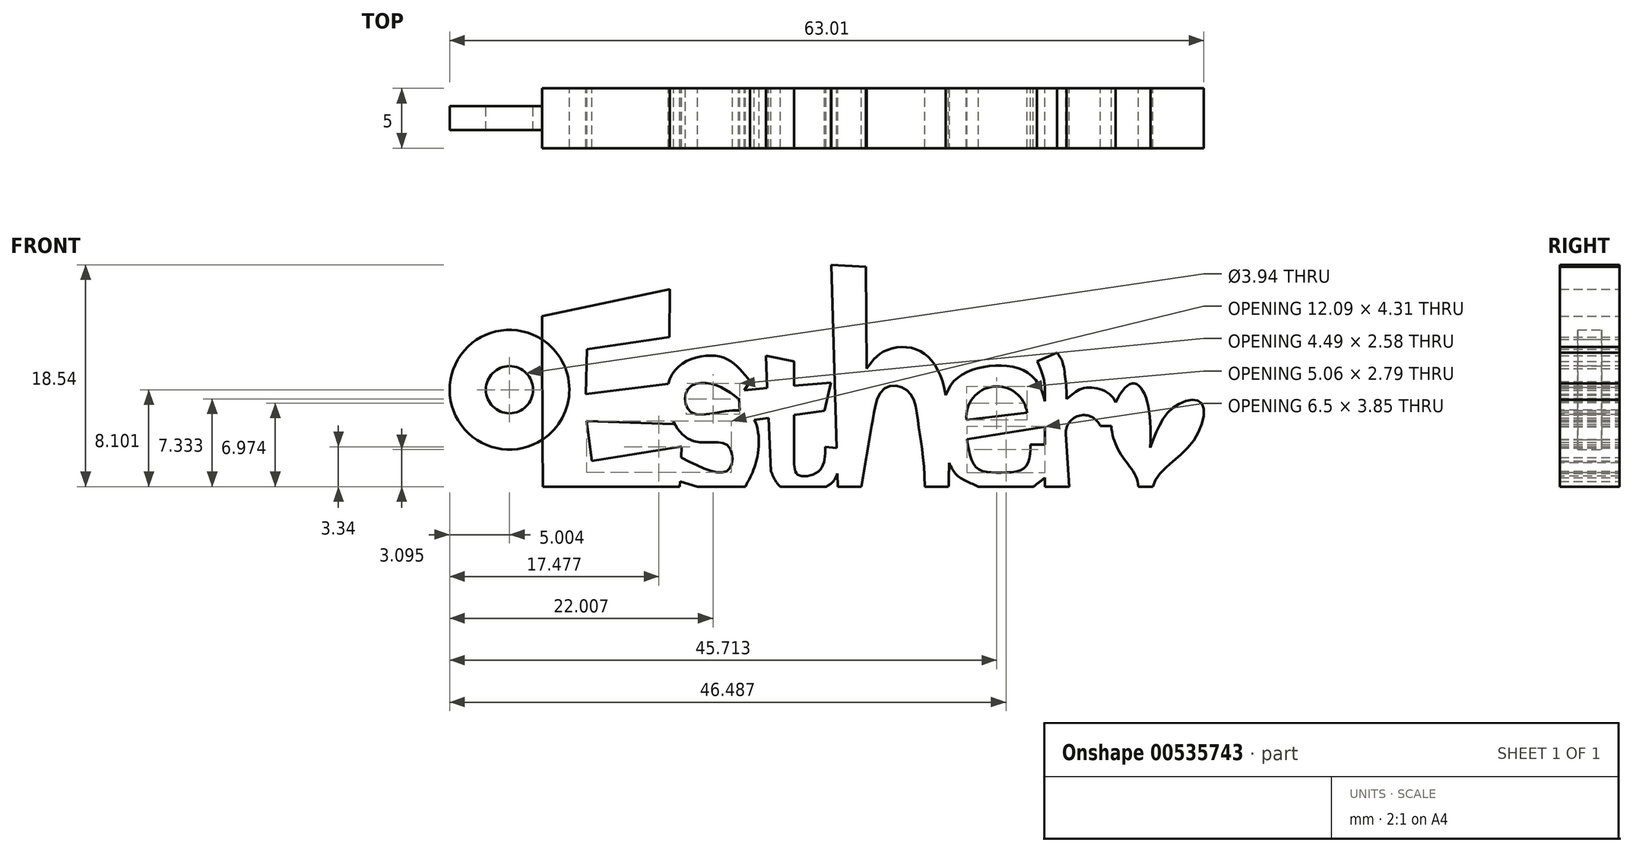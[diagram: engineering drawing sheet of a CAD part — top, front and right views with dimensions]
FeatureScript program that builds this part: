
annotation { "Feature Type Name" : "Feature", "Feature Type Description" : "" }
export const myFeature = defineFeature(function(context is Context, id is Id, definition is map)
    precondition{}
    {
        {
            var Q0;
            Q0=qCreatedBy(makeId("Front.planeOp"),FACE);
            var sketch = newSketch(context, id + "F0", { "sketchPlane" : qUnion([Q0])});
            skLineSegment(sketch, "E0", {"start": v(-25.3, 9.16) * mm, "end": v(-14.64, 11.43) * mm});
            skLineSegment(sketch, "E1", {"start": v(-14.64, 11.43) * mm, "end": v(-14.65, 7.42) * mm});
            skLineSegment(sketch, "E2", {"start": v(-14.65, 7.42) * mm, "end": v(-21.53, 6.42) * mm});
            skLineSegment(sketch, "E3", {"start": v(-21.53, 6.42) * mm, "end": v(-21.65, 2.67) * mm});
            skLineSegment(sketch, "E4", {"start": v(-21.65, 2.67) * mm, "end": v(-14.37, 3.56) * mm});
            skLineSegment(sketch, "E5", {"start": v(-14.37, 3.56) * mm, "end": v(-14.31, 0.15) * mm});
            skLineSegment(sketch, "E6", {"start": v(-14.31, 0.15) * mm, "end": v(-21.59, 0.43) * mm});
            skLineSegment(sketch, "E7", {"start": v(-21.59, 0.43) * mm, "end": v(-21.14, -2.93) * mm});
            skLineSegment(sketch, "E8", {"start": v(-21.14, -2.93) * mm, "end": v(-13.64, -1.7) * mm});
            skLineSegment(sketch, "E9", {"start": v(-13.64, -1.7) * mm, "end": v(-13.8, -5.07) * mm});
            skLineSegment(sketch, "E10", {"start": v(-13.8, -5.07) * mm, "end": v(-25.23, -5.07) * mm});
            skLineSegment(sketch, "E11", {"start": v(-25.23, -5.07) * mm, "end": v(-25.3, 9.16) * mm});
            skFitSpline(sketch, "E12", {"points": [v(-7.93, 3.73) * mm, v(-10.44, 5.8) * mm, v(-14.53, 4.12) * mm, v(-13.08, -1.09) * mm, v(-9.83, -1.6) * mm, v(-9.72, -3.67) * mm, v(-13.97, -2.49) * mm], "startDerivative": vector(-13.02, 17.28) * mm, "endDerivative": vector(-29.51, 15.15) * mm});
            skLineSegment(sketch, "E13", {"start": v(-13.97, -2.49) * mm, "end": v(-15.5, -5.07) * mm});
            skLineSegment(sketch, "E14", {"start": v(-15.5, -5.07) * mm, "end": v(-8.32, -5.07) * mm});
            skLineSegment(sketch, "E15", {"start": v(-7.93, 3.73) * mm, "end": v(-8.88, 2.27) * mm});
            skFitSpline(sketch, "E16", {"points": [v(-8.88, 2.27) * mm, v(-11.06, 3.5) * mm, v(-13.13, 3.05) * mm, v(-12.74, 1.1) * mm, v(-8.26, 1.19) * mm, v(-7.25, -2.27) * mm, v(-8.32, -5.07) * mm], "startDerivative": vector(-12.95, 9.86) * mm, "endDerivative": vector(-8.13, -15.9) * mm});
            skLineSegment(sketch, "E17", {"start": v(-8.4, 3) * mm, "end": v(-1.15, 3.61) * mm});
            skLineSegment(sketch, "E18", {"start": v(-1.15, 3.61) * mm, "end": v(-1.71, 1.26) * mm});
            skLineSegment(sketch, "E19", {"start": v(-8.88, 3) * mm, "end": v(-8.4, 3) * mm});
            skLineSegment(sketch, "E20", {"start": v(-6.6, 5.86) * mm, "end": v(-4.25, 5.39) * mm});
            skLineSegment(sketch, "E21", {"start": v(-4.25, 5.39) * mm, "end": v(-4.25, -3) * mm});
            skLineSegment(sketch, "E22", {"start": v(-6.6, 5.86) * mm, "end": v(-6.18, -3.8) * mm});
            skFitSpline(sketch, "E23", {"points": [v(-6.18, -3.8) * mm, v(-5.04, -5.32) * mm, v(-2.45, -5.32) * mm, v(-0.87, -4.5) * mm, v(-0.33, -2.33) * mm, v(-0.38, -1.86) * mm], "startDerivative": vector(3.98, -8.84) * mm, "endDerivative": vector(-0.72, 3.35) * mm});
            skLineSegment(sketch, "E24", {"start": v(-1.63, -1.74) * mm, "end": v(-0.38, -1.86) * mm});
            skFitSpline(sketch, "E25", {"points": [v(-4.25, -3) * mm, v(-3.89, -4.1) * mm, v(-2.14, -3.74) * mm, v(-1.63, -1.74) * mm], "startDerivative": vector(0.2, -4.88) * mm, "endDerivative": vector(0.09, 6.18) * mm});
            skLineSegment(sketch, "E26", {"start": v(-8.88, 3) * mm, "end": v(-8.71, 0.36) * mm});
            skLineSegment(sketch, "E27", {"start": v(-8.32, -5.07) * mm, "end": v(34.22, -5.07) * mm});
            skLineSegment(sketch, "E28", {"start": v(34.22, -5.07) * mm, "end": v(34.22, -5.7) * mm});
            skLineSegment(sketch, "E29", {"start": v(-1.71, 1.26) * mm, "end": v(-8.71, 0.36) * mm});
            skLineSegment(sketch, "E30", {"start": v(-1.14, 13.47) * mm, "end": v(-0.59, -5.32) * mm});
            skLineSegment(sketch, "E31", {"start": v(-0.59, -5.32) * mm, "end": v(1.37, -5.07) * mm});
            skLineSegment(sketch, "E32", {"start": v(1.37, -5.07) * mm, "end": v(2.25, 0) * mm});
            skLineSegment(sketch, "E33", {"start": v(-1.14, 13.47) * mm, "end": v(1.74, 13.3) * mm});
            skLineSegment(sketch, "E34", {"start": v(1.74, 13.3) * mm, "end": v(1.84, 4.79) * mm});
            skFitSpline(sketch, "E35", {"points": [v(2.25, 0) * mm, v(3.2, 3.04) * mm, v(5.27, 2.9) * mm, v(6.17, 0) * mm, v(6.69, -5.07) * mm], "startDerivative": vector(1.76, 9.63) * mm, "endDerivative": vector(0.27, -22.07) * mm});
            skFitSpline(sketch, "E36", {"points": [v(1.84, 4.79) * mm, v(3.2, 6.2) * mm, v(5.89, 6.43) * mm, v(8.1, 3.9) * mm, v(8.66, -5.07) * mm], "startDerivative": vector(6.3, 9.08) * mm, "endDerivative": vector(-0.74, -27.4) * mm});
            skLineSegment(sketch, "E37", {"start": v(10.22, -1.1) * mm, "end": v(17, 0) * mm});
            skFitSpline(sketch, "E38", {"points": [v(17, 0) * mm, v(15.82, 3.99) * mm, v(12.24, 5.02) * mm, v(8.85, 3.42) * mm, v(8.05, -0.91) * mm], "startDerivative": vector(-1.1, 14.93) * mm, "endDerivative": vector(-0.27, -18.01) * mm});
            skFitSpline(sketch, "E39", {"points": [v(8.05, -0.91) * mm, v(9.28, -4.02) * mm, v(11.16, -5.07) * mm], "startDerivative": vector(1.72, -6.44) * mm, "endDerivative": vector(4.58, -2.3) * mm});
            skLineSegment(sketch, "E40", {"start": v(15.5, -1.57) * mm, "end": v(17.07, -1.57) * mm});
            skArc(sketch, "E41", {"start": v(15.22, 1.1) * mm, "mid": v(12.4, 3.3) * mm, "end": v(10.16, 0.51) * mm});
            skLineSegment(sketch, "E42", {"start": v(10.16, 0.51) * mm, "end": v(15.22, 1.1) * mm});
            skFitSpline(sketch, "E43", {"points": [v(10.22, -1.1) * mm, v(10.98, -3.47) * mm, v(13.01, -3.9) * mm, v(15.08, -3.43) * mm, v(15.5, -1.57) * mm], "startDerivative": vector(1.46, -10.58) * mm, "endDerivative": vector(0.22, 9.33) * mm});
            skFitSpline(sketch, "E44", {"points": [v(17.07, -1.57) * mm, v(17.07, -3.83) * mm, v(15.74, -5.07) * mm], "startDerivative": vector(0.71, -4.73) * mm, "endDerivative": vector(-3.43, -2.68) * mm});
            skLineSegment(sketch, "E45", {"start": v(16.72, 3.15) * mm, "end": v(16.72, -5.07) * mm});
            skLineSegment(sketch, "E46", {"start": v(16.72, -5.07) * mm, "end": v(16.83, -5.26) * mm});
            skLineSegment(sketch, "E47", {"start": v(16.05, 5.41) * mm, "end": v(17.74, 6.12) * mm});
            skFitSpline(sketch, "E48", {"points": [v(17.74, 6.12) * mm, v(18.16, 5.39) * mm, v(18.53, 2.26) * mm], "startDerivative": vector(1.63, -2.78) * mm, "endDerivative": vector(0.11, -5.24) * mm});
            skFitSpline(sketch, "E49", {"points": [v(16.05, 5.41) * mm, v(16.4, 4.66) * mm, v(16.72, 3.15) * mm], "startDerivative": vector(1.1, -1.78) * mm, "endDerivative": vector(0.14, -3.33) * mm});
            skLineSegment(sketch, "E50", {"start": v(18.47, -0.68) * mm, "end": v(18.74, -5.07) * mm});
            skArc(sketch, "E51", {"start": v(21.33, 0) * mm, "mid": v(19.61, 0.87) * mm, "end": v(18.47, -0.68) * mm});
            skLineSegment(sketch, "E52", {"start": v(22.97, 0) * mm, "end": v(21.33, 0) * mm});
            skFitSpline(sketch, "E53", {"points": [v(18.53, 2.26) * mm, v(20.08, 3.18) * mm, v(22.36, 2.42) * mm, v(22.97, 0) * mm], "startDerivative": vector(5, 3.96) * mm, "endDerivative": vector(0.8, -6.84) * mm});
            skFitSpline(sketch, "E54", {"points": [v(24.52, -5.07) * mm, v(23.14, -2.47) * mm, v(22.3, 0.8) * mm, v(23.81, 3.5) * mm, v(24.8, 3.1) * mm, v(25.5, -1.82) * mm], "startDerivative": vector(-0.48, 14.78) * mm, "endDerivative": vector(-1.96, -25.42) * mm});
            skFitSpline(sketch, "E55", {"points": [v(25.5, -1.82) * mm, v(27.37, 1.49) * mm, v(29.71, 1.99) * mm, v(29.04, -1.34) * mm, v(25.72, -5.07) * mm], "startDerivative": vector(6.34, 15.81) * mm, "endDerivative": vector(-2.63, -13.8) * mm});
            skLineSegment(sketch, "E56", {"start": v(-25.29, 6.06) * mm, "end": v(-25.26, 0.05) * mm});
            skLineSegment(sketch, "E57.bottom", {"start": v(-25.29, 6.06) * mm, "end": v(-27.26, 6.06) * mm});
            skLineSegment(sketch, "E57.top", {"start": v(-25.29, 0) * mm, "end": v(-27.26, 0) * mm});
            skLineSegment(sketch, "E57.left", {"start": v(-25.29, 6.06) * mm, "end": v(-25.29, 0) * mm});
            skLineSegment(sketch, "E57.right", {"start": v(-27.26, 6.06) * mm, "end": v(-27.26, 0) * mm});
            skCircle(sketch, "E58", {"center": v(-28.02, 3.03) * mm, "radius": 1.97 * mm});
            skPoint(sketch, "E58.centerSnap0", {"position": v(-27.26, 3.03) * mm});
            skCircle(sketch, "E59", {"center": v(-28.02, 3.03) * mm, "radius": 5 * mm});
            skLineSegment(sketch, "E60", {"start": v(-13.78, -4.63) * mm, "end": v(-12.3, -5.07) * mm});
            skSolve(sketch);
        }
        {
            var Q0;
            Q0=makeQuery(id+"F0.imprint","IMPRINT",FACE,{"disambiguationData":[TD([[makeQuery(id+"F0.imprint","IMPRINT",EDGE,{"derivedFrom":sQuery(id+"F0.wireOp",EDGE,"E0")}),-1.0]])]});
            var Q1;
            {var subQ0=sQuery(id+"F0.wireOp",EDGE,"E14");var subQ1=sQuery(id+"F0.wireOp",EDGE,"E9");var subQ2=makeQuery(id+"F0.imprint","INTERSECT",VERTEX,{"derivedFrom":[subQ1,subQ0]});Q1=makeQuery(id+"F0.imprint","IMPRINT",FACE,{"disambiguationData":[TD([[makeQuery(id+"F0.imprint","IMPRINT",EDGE,{"disambiguationData":[TD([[subQ2,1.0]])],"derivedFrom":subQ1}),-1.0]])]});}
            var Q2;
            {var subQ10=sQuery(id+"F0.wireOp",EDGE,"E12");Q2=makeQuery(id+"F0.imprint","IMPRINT",FACE,{"disambiguationData":[TD([[makeQuery(id+"F0.imprint","IMPRINT",EDGE,{"derivedFrom":subQ10}),1.0]])]});}
            var Q3;
            {var subQ0=sQuery(id+"F0.wireOp",EDGE,"E19");Q3=makeQuery(id+"F0.imprint","IMPRINT",FACE,{"disambiguationData":[TD([[makeQuery(id+"F0.imprint","IMPRINT",EDGE,{"derivedFrom":subQ0}),-1.0]])]});}
            var Q4;
            {var subQ0=sQuery(id+"F0.wireOp",EDGE,"E26");var subQ1=sQuery(id+"F0.wireOp",EDGE,"E16");var subQ2=makeQuery(id+"F0.imprint","INTERSECT",VERTEX,{"derivedFrom":[subQ1,subQ0]});Q4=makeQuery(id+"F0.imprint","IMPRINT",FACE,{"disambiguationData":[TD([[makeQuery(id+"F0.imprint","IMPRINT",EDGE,{"disambiguationData":[TD([[subQ2,-1.0]])],"derivedFrom":subQ1}),-1.0]])]});}
            var Q5;
            {var subQ0=sQuery(id+"F0.wireOp",EDGE,"E26");var subQ1=sQuery(id+"F0.wireOp",EDGE,"E16");var subQ2=makeQuery(id+"F0.imprint","INTERSECT",VERTEX,{"derivedFrom":[subQ1,subQ0]});Q5=makeQuery(id+"F0.imprint","IMPRINT",FACE,{"disambiguationData":[TD([[makeQuery(id+"F0.imprint","IMPRINT",EDGE,{"disambiguationData":[TD([[subQ2,-1.0]])],"derivedFrom":subQ1}),1.0]])]});}
            var Q6;
            {var subQ0=sQuery(id+"F0.wireOp",EDGE,"E22");var subQ1=sQuery(id+"F0.wireOp",EDGE,"E17");var subQ2=makeQuery(id+"F0.imprint","INTERSECT",VERTEX,{"derivedFrom":[subQ1,subQ0]});Q6=makeQuery(id+"F0.imprint","IMPRINT",FACE,{"disambiguationData":[TD([[makeQuery(id+"F0.imprint","IMPRINT",EDGE,{"disambiguationData":[TD([[subQ2,-1.0]])],"derivedFrom":subQ1}),-1.0]])]});}
            var Q7;
            {var subQ5=sQuery(id+"F0.wireOp",EDGE,"E20");Q7=makeQuery(id+"F0.imprint","IMPRINT",FACE,{"disambiguationData":[TD([[makeQuery(id+"F0.imprint","IMPRINT",EDGE,{"derivedFrom":subQ5}),-1.0]])]});}
            var Q8;
            {var subQ0=sQuery(id+"F0.wireOp",EDGE,"E18");Q8=makeQuery(id+"F0.imprint","IMPRINT",FACE,{"disambiguationData":[TD([[makeQuery(id+"F0.imprint","IMPRINT",EDGE,{"derivedFrom":subQ0}),-1.0]])]});}
            var Q9;
            {var subQ12=sQuery(id+"F0.wireOp",EDGE,"E25");Q9=makeQuery(id+"F0.imprint","IMPRINT",FACE,{"disambiguationData":[TD([[makeQuery(id+"F0.imprint","IMPRINT",EDGE,{"derivedFrom":subQ12}),-1.0]])]});}
            var Q10;
            {var subQ0=sQuery(id+"F0.wireOp",EDGE,"E24");var subQ1=sQuery(id+"F0.wireOp",EDGE,"E23");var subQ2=makeQuery(id+"F0.imprint","INTERSECT",VERTEX,{"derivedFrom":[subQ1,subQ0]});Q10=makeQuery(id+"F0.imprint","IMPRINT",FACE,{"disambiguationData":[TD([[makeQuery(id+"F0.imprint","IMPRINT",EDGE,{"disambiguationData":[TD([[subQ2,1.0]])],"derivedFrom":subQ1}),1.0]])]});}
            var Q11;
            {var subQ3=sQuery(id+"F0.wireOp",EDGE,"E32");Q11=makeQuery(id+"F0.imprint","IMPRINT",FACE,{"disambiguationData":[TD([[makeQuery(id+"F0.imprint","IMPRINT",EDGE,{"derivedFrom":subQ3}),1.0]])]});}
            var Q12;
            {var subQ0=sQuery(id+"F0.wireOp",EDGE,"E38");var subQ1=sQuery(id+"F0.wireOp",EDGE,"E36");var subQ2=makeQuery(id+"F0.imprint","INTERSECT",VERTEX,{"derivedFrom":[subQ1,subQ0]});Q12=makeQuery(id+"F0.imprint","IMPRINT",FACE,{"disambiguationData":[TD([[makeQuery(id+"F0.imprint","IMPRINT",EDGE,{"disambiguationData":[TD([[subQ2,-1.0]])],"derivedFrom":subQ1}),-1.0]])]});}
            var Q13;
            Q13=makeQuery(id+"F0.imprint","IMPRINT",FACE,{"disambiguationData":[TD([[makeQuery(id+"F0.imprint","IMPRINT",EDGE,{"derivedFrom":sQuery(id+"F0.wireOp",EDGE,"E41")}),-1.0]])]});
            var Q14;
            {var subQ0=sQuery(id+"F0.wireOp",EDGE,"E38");var subQ1=sQuery(id+"F0.wireOp",EDGE,"E37");var subQ2=makeQuery(id+"F0.imprint","INTERSECT",VERTEX,{"derivedFrom":[subQ1,subQ0]});Q14=makeQuery(id+"F0.imprint","IMPRINT",FACE,{"disambiguationData":[TD([[makeQuery(id+"F0.imprint","IMPRINT",EDGE,{"disambiguationData":[TD([[subQ2,1.0]])],"derivedFrom":subQ1}),1.0]])]});}
            var Q15;
            {var subQ0=sQuery(id+"F0.wireOp",EDGE,"E44");var subQ1=sQuery(id+"F0.wireOp",EDGE,"E40");var subQ2=makeQuery(id+"F0.imprint","INTERSECT",VERTEX,{"derivedFrom":[subQ1,subQ0]});Q15=makeQuery(id+"F0.imprint","IMPRINT",FACE,{"disambiguationData":[TD([[makeQuery(id+"F0.imprint","IMPRINT",EDGE,{"disambiguationData":[TD([[subQ2,1.0]])],"derivedFrom":subQ1}),-1.0]])]});}
            var Q16;
            Q16=makeQuery(id+"F0.imprint","IMPRINT",FACE,{"disambiguationData":[TD([[makeQuery(id+"F0.imprint","IMPRINT",EDGE,{"derivedFrom":sQuery(id+"F0.wireOp",EDGE,"E47")}),-1.0]])]});
            var Q17;
            {var subQ7=sQuery(id+"F0.wireOp",EDGE,"E55");Q17=makeQuery(id+"F0.imprint","IMPRINT",FACE,{"disambiguationData":[TD([[makeQuery(id+"F0.imprint","IMPRINT",EDGE,{"derivedFrom":subQ7}),-1.0]])]});}
            var Q18;
            {var subQ0=sQuery(id+"F0.wireOp",EDGE,"E53");var subQ1=sQuery(id+"F0.wireOp",EDGE,"E52");var subQ2=makeQuery(id+"F0.imprint","INTERSECT",VERTEX,{"derivedFrom":[subQ1,subQ0]});Q18=makeQuery(id+"F0.imprint","IMPRINT",FACE,{"disambiguationData":[TD([[makeQuery(id+"F0.imprint","IMPRINT",EDGE,{"disambiguationData":[TD([[subQ2,-1.0]])],"derivedFrom":subQ1}),-1.0]])]});}
            var Q19;
            {var subQ0=sQuery(id+"F0.wireOp",EDGE,"E5");var subQ1=sQuery(id+"F0.wireOp",EDGE,"E4");var subQ2=makeQuery(id+"F0.imprint","INTERSECT",VERTEX,{"derivedFrom":[subQ1,subQ0]});Q19=makeQuery(id+"F0.imprint","IMPRINT",FACE,{"disambiguationData":[TD([[makeQuery(id+"F0.imprint","IMPRINT",EDGE,{"disambiguationData":[TD([[subQ2,1.0]])],"derivedFrom":subQ1}),-1.0]])]});}
            var Q20;
            {var subQ0=sQuery(id+"F0.wireOp",EDGE,"Ady5i4Xr-irVW-KI9F-AB6i-uTljDv2ZzF0V");Q20=makeQuery(id+"F0.imprint","IMPRINT",FACE,{"disambiguationData":[TD([[makeQuery(id+"F0.imprint","IMPRINT",EDGE,{"derivedFrom":subQ0}),1.0]])]});}
            var Q21;
            Q21=makeQuery(id+"F0.imprint","IMPRINT",FACE,{"disambiguationData":[TD([[makeQuery(id+"F0.imprint","IMPRINT",EDGE,{"derivedFrom":sQuery(id+"F0.wireOp",EDGE,"Kfr6fFeU-wD7T-IBrD-V54f-2WappjVIHJ6v")}),-1.0]])]});
            var Q22;
            {var subQ0=sQuery(id+"F0.wireOp",EDGE,"E59");var subQ1=sQuery(id+"F0.wireOp",EDGE,"E56");var subQ2=makeQuery(id+"F0.imprint","INTERSECT",VERTEX,{"disambiguationData":[OD(0.0)],"derivedFrom":[subQ1,subQ0]});Q22=makeQuery(id+"F0.imprint","IMPRINT",FACE,{"disambiguationData":[TD([[makeQuery(id+"F0.imprint","IMPRINT",EDGE,{"disambiguationData":[TD([[subQ2,1.0]])],"derivedFrom":subQ1}),1.0]])]});}
            extrude(context, id + "F1", {"entities" : qUnion([Q0, Q1, Q2, Q3, Q4, Q5, Q6, Q7, Q8, Q9, Q10, Q11, Q12, Q13, Q14, Q15, Q16, Q17, Q18, Q19, Q20, Q21, Q22]), "depth" : 5 * mm, "offsetDistance" : 25 * mm});
        }
        {
            var Q0;
            {var subQ0=sQuery(id+"F0.wireOp",EDGE,"E57.right");var subQ5=sQuery(id+"F0.wireOp",EDGE,"E57.bottom");var subQ6=makeQuery(id+"F0.imprint","INTERSECT",VERTEX,{"derivedFrom":[subQ5,subQ0]});Q0=makeQuery(id+"F0.imprint","IMPRINT",FACE,{"disambiguationData":[TD([[makeQuery(id+"F0.imprint","IMPRINT",EDGE,{"disambiguationData":[TD([[subQ6,1.0]])],"derivedFrom":subQ5}),-1.0]])]});}
            var Q1;
            {var subQ0=sQuery(id+"F0.wireOp",EDGE,"E57.right");var subQ1=sQuery(id+"F0.wireOp",EDGE,"E57.bottom");var subQ2=makeQuery(id+"F0.imprint","INTERSECT",VERTEX,{"derivedFrom":[subQ1,subQ0]});Q1=makeQuery(id+"F0.imprint","IMPRINT",FACE,{"disambiguationData":[TD([[makeQuery(id+"F0.imprint","IMPRINT",EDGE,{"disambiguationData":[TD([[subQ2,1.0]])],"derivedFrom":subQ1}),1.0]])]});}
            var Q2;
            {var subQ1=sQuery(id+"F0.wireOp",EDGE,"E57.bottom");var subQ3=sQuery(id+"F0.wireOp",EDGE,"E59");var subQ4=makeQuery(id+"F0.imprint","INTERSECT",VERTEX,{"derivedFrom":[subQ1,subQ3]});Q2=makeQuery(id+"F0.imprint","IMPRINT",FACE,{"disambiguationData":[TD([[makeQuery(id+"F0.imprint","IMPRINT",EDGE,{"disambiguationData":[TD([[subQ4,1.0]])],"derivedFrom":subQ3}),-1.0]])]});}
            var Q3;
            {var subQ0=sQuery(id+"F0.wireOp",EDGE,"E57.left");var subQ1=sQuery(id+"F0.wireOp",EDGE,"E57.top");var subQ2=makeQuery(id+"F0.imprint","INTERSECT",VERTEX,{"derivedFrom":[subQ1,subQ0]});Q3=makeQuery(id+"F0.imprint","IMPRINT",FACE,{"disambiguationData":[TD([[makeQuery(id+"F0.imprint","IMPRINT",EDGE,{"disambiguationData":[TD([[subQ2,-1.0]])],"derivedFrom":subQ1}),-1.0]])]});}
            var Q4;
            {var subQ0=sQuery(id+"F0.wireOp",EDGE,"E56");Q4=makeQuery(id+"F0.imprint","IMPRINT",FACE,{"disambiguationData":[TD([[makeQuery(id+"F0.imprint","IMPRINT",EDGE,{"derivedFrom":subQ0}),1.0]])]});}
            extrude(context, id + "F2", {"entities" : qUnion([Q0, Q1, Q2, Q3, Q4]), "operationType" : NewBodyOperationType.ADD, "depth" : 3.5 * mm, "offsetDistance" : 25 * mm, "hasSecondDirection" : true, "secondDirectionOppositeDirection" : false, "secondDirectionDepth" : 1.5 * mm});
        }
    });
